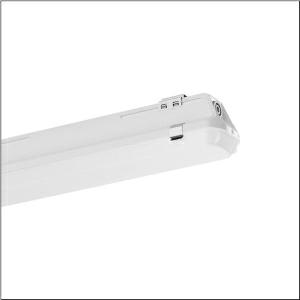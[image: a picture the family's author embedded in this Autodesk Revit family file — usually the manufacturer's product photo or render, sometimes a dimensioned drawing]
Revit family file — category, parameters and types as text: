
# Revit family: monsun_r__11_51fp12mp480h_cfdd
name_source: partatom
category: Lighting Fixtures
units: mm (PartAtom-declared; Revit-internal decimal feet)

## family parameters
Cut with Voids When Loaded = No
Host = Face
Light Source = No
Part Type = Normal
Room Calculation Point = No
Round Connector Dimension = Use Diameter
Shared = No

## types (1)
- --- (1 x LED, 7990 lm, 45.4 W, 4000K)
    Apparent Load = 45 VA
    CIE Flux Codes = 65 88 97 97 100
    Color Rendering = 80
    Color Temperature = 4000K
    Default Elevation = 1800 mm
    Description = Monsun® 11, damp-proof luminaire, chain hanger, primary light control with lens, primary optical cover: enclosure, of PMMA, light emission: direct distribution, primary light characteristic: symmetric, installation type: suspended mounting, surface-mounted, horizontal mounting, vertical mounting, LED, rated luminous flux: 7.990lm, luminous efficacy: 176lm/W, light colour: 840, colour temperature: 4000K, control gear: ECG, with terminal, 3-pole, max. 2.5mm², mains connection: 220..240V, AC, 50/60Hz, rated input power: 45W, luminaire housing, of glass-fibre reinforced polyester, uncoated, bright grey, incl. chain hanger, length: 1.590mm, width: 90mm, height: 88mm, clip for enclosure, of stainless steel (V2A), ceiling mounting element, of stainless steel (V2A), chain hanger, of stainless steel (V2A), protection rating (complete): IP66, insulation class (complete): insulation class I (protective earthing), certification: CE, ENEC, VDE, UKCA, protection symbol: D, impact resistance: IK04, permissible operating ambient temperature: -35..+40°C, standard: EN 50419, EN 60598-2-1, no direct snow, no direct sun, no direct rain, for indoor or canopied outdoor use, corresponds to IFS (International Featured Standards) requirements for safety and quality in the food industry, contact your sales advisor before using the luminaires in applications with unclear chemical exposure, large temperature fluctuations or condensation-forming humidity, LABS conformity tested according to VDMA 24364:2018-05, packaging unit: 1 piece
    Height = 89 mm
    Lamp = 1 x LED
    Lamp Light Flux = 7990 lm
    Lamp Power = 45.4 W
    Lamp count = 1
    Length = 1590 mm
    Luminous efficacy = 176 lm/W
    Manufacturer = Siteco
    ModVariant = No
    Model = 51FP12MP480H
    Mounting Place = Ceiling
    Mounting Type = Surface mounted
    Number of Poles = 1
    OnlyDefault = Yes
    Power Factor = 1
    Product Name = Monsun® 11
    Product group = damp-proof luminaire
    ProductGroupID = 301
    Protection Class = Protection class I
    Protection Degree = IP 66
    RLX_Detail_Level = 1
    RLX_Emergency_Light_Flux = 0 lm
    RLX_Emergency_Type = 0
    RLX_Emergency_Type_DB = No
    RlxData = <blob elided: 89981 chars, md5=2fae576d>
    Socket = socket
    Standby Power = 0 W
    System Light Flux = 7990 lm
    System Power = 45 W
    Type Comments = factory setting: luminous flux: 100 % | (A | C | E) | 105 mA
    Type Image = l_1004748.jpg
    URL = http://relux.com
    VarID = @adj_157121
    Voltage = 0 V
    Weight = 0.00 kg
    Width = 90 mm

## geometry (parser evidence)
native form markers: Blend x4, Sweep x10
no freeform markers — native parametric forms only
